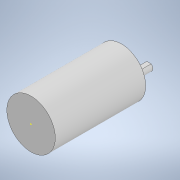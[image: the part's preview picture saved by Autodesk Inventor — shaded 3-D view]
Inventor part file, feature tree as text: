
AUTODESK INVENTOR PART (.ipt)
format: ipt  version: 2020.2 (Build 242310000, 310)  size: 137,216 bytes
history: native  units: mm
features: sketch x5, extrude x4, hole x1
ambient origin geometry x8: Origin, YZ Plane, XZ Plane, XY Plane, X Axis, Y Axis, Z Axis, Center Point
bodies: Solido1 (feature_tree)
feature tree (10):
  extrude  "Estrusione1"  Depth=37.0mm
  hole  "Foro1"  [1 undecoded]
  extrude  "Estrusione2"  Depth=15.3mm
  extrude  "Estrusione3"  TaperAngle=0.0deg  [1 undecoded]
  extrude  "Estrusione4"  Depth=60.0mm TaperAngle=360.0deg
  sketch  "Schizzo6"
  sketch  "Schizzo1"
  sketch  "Schizzo2"
  sketch  "Schizzo4"
  sketch  "Schizzo5"
note: 2 required parameter values undecoded (feature->parameter linkage not recoverable at this tier; creation-order binding heuristic only, values carry confidence <= 0.55)
